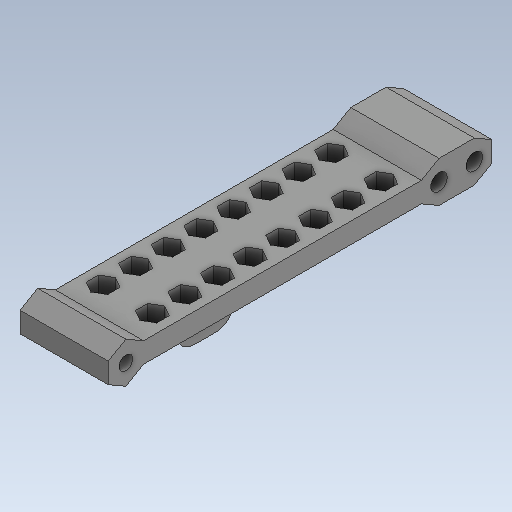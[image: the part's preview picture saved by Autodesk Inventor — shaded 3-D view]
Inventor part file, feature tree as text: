
AUTODESK INVENTOR PART (.ipt)
format: ipt  version: 2020 (Build 240168000, 168)  size: 571,392 bytes
history: native  units: in
note: dims shown in document units (in); Inventor stores cm internally (conversion verified against a paired STEP export)
features: sketch x7, extrude x6, projected_geometry x4, plane x2, mirror x1, fillet x1
ambient origin geometry x8: Origin, YZ Plane, XZ Plane, XY Plane, X Axis, Y Axis, Z Axis, Center Point
bodies: Solid1 (feature_tree)
feature tree (21):
  extrude  "Extrusion1"  Depth=3.4256in
  plane  "Work Plane1"
  extrude  "Extrusion2"  Depth=0.7874in
  sketch  "Sketch4"  dims[d4=0.0in d5=0.0906in]
  extrude  "Extrusion4"  Depth=0.0906in
  plane  "Work Plane2"
  extrude  "Extrusion6"  Depth=3.1106in
  mirror  "Mirror2"
  extrude  "Extrusion7"  Depth=0.315in
  extrude  "Extrusion8"  Depth=0.2362in
  fillet  "Fillet1"  [1 undecoded]
  sketch  "Sketch1"  dims[d0=0.1818in d1=3.4256in]
  sketch  "Sketch2"  dims[d2=0.122in d3=0.7874in]
  sketch  "Sketch5"  dims[d6=0.7874in d7=0.0in d28=3.1106in]
  sketch  "Sketch7"  dims[d29=0.315in d31=0.315in]
  projected_geometry  "Projected Loop7"
  projected_geometry  "Projected Loop8"
  sketch  "Sketch8"  dims[d33=0.1476in d34=0.2362in d35=0.0in]
  projected_geometry  "Projected Loop9"
  sketch  "Sketch10"  dims[d38=0.315in d39=0.2756in d40=-0.3092in d41=0.0787in d42=0.0787in d43=0.0787in d44=3.1496in d46=0.2913in d47=0.3937in d49=0.3937in d51=3.1496in d53=0.2913in d54=0.3937in d56=0.3937in d58=0.0in d59=0.0in d60=1.0994in d61=0.1378in d63=1.1811in d64=0.1575in d65=0.0in d66=0.126in d67=0.1575in d69=2.4807in]
  projected_geometry  "Projected Loop10"
note: 1 required parameter value undecoded (feature->parameter linkage not recoverable at this tier; creation-order binding heuristic only, values carry confidence <= 0.55)
